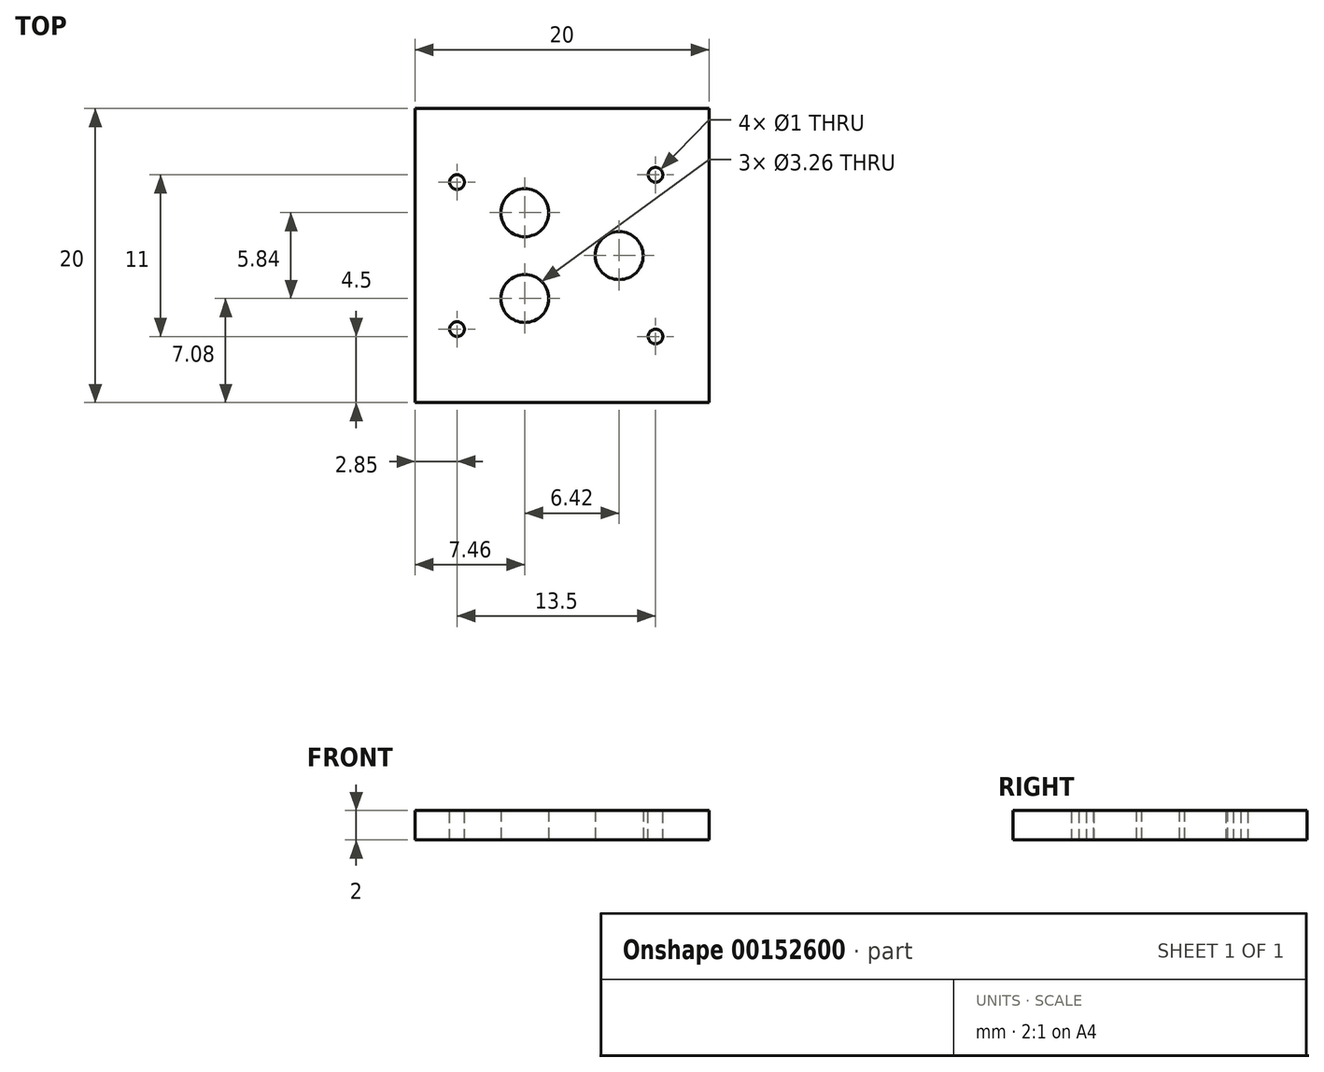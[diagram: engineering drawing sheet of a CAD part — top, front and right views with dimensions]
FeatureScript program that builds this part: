
annotation { "Feature Type Name" : "Feature", "Feature Type Description" : "" }
export const myFeature = defineFeature(function(context is Context, id is Id, definition is map)
    precondition{}
    {
        {
            var Q0;
            Q0=qCreatedBy(makeId("Top.planeOp"),FACE);
            var sketch = newSketch(context, id + "F0", { "sketchPlane" : qUnion([Q0])});
            skLineSegment(sketch, "E0.bottom", {"start": v(-10, 10) * mm, "end": v(10, 10) * mm});
            skLineSegment(sketch, "E0.top", {"start": v(-10, -10) * mm, "end": v(10, -10) * mm});
            skLineSegment(sketch, "E0.left", {"start": v(-10, 10) * mm, "end": v(-10, -10) * mm});
            skLineSegment(sketch, "E0.right", {"start": v(10, 10) * mm, "end": v(10, -10) * mm});
            skPoint(sketch, "E0.middle", {"position": v(0, 0) * mm});
            skCircle(sketch, "E1", {"center": v(-2.54, 2.92) * mm, "radius": 1.63 * mm});
            skCircle(sketch, "E2", {"center": v(-2.54, -2.92) * mm, "radius": 1.63 * mm});
            skCircle(sketch, "E3", {"center": v(3.88, 0) * mm, "radius": 1.63 * mm});
            skSolve(sketch);
        }
        {
            var Q0;
            Q0=makeQuery(id+"F0.imprint","IMPRINT",FACE,{"disambiguationData":[TD([[makeQuery(id+"F0.imprint","IMPRINT",EDGE,{"derivedFrom":sQuery(id+"F0.wireOp",EDGE,"E0.bottom")}),-1.0]])]});
            extrude(context, id + "F1", {"entities" : qUnion([Q0]), "depth" : 2 * mm});
        }
        {
            var Q0;
            Q0=makeQuery(id+"F1.opExtrude","CAP_FACE",FACE,{"disambiguationData":[OSD([sQuery(id+"F0.wireOp",EDGE,"E0.bottom"),sQuery(id+"F0.wireOp",EDGE,"E0.top"),sQuery(id+"F0.wireOp",EDGE,"E0.left"),sQuery(id+"F0.wireOp",EDGE,"E0.right"),sQuery(id+"F0.wireOp",EDGE,"E1"),sQuery(id+"F0.wireOp",EDGE,"E2"),sQuery(id+"F0.wireOp",EDGE,"E3")])],"isStart":false});
            var sketch = newSketch(context, id + "F2", { "sketchPlane" : qUnion([Q0])});
            skLineSegment(sketch, "E4.bottom", {"start": v(5, 5) * mm, "end": v(-5, 5) * mm});
            skLineSegment(sketch, "E4.top", {"start": v(5, -5) * mm, "end": v(-5, -5) * mm});
            skLineSegment(sketch, "E4.right", {"start": v(-5, 5) * mm, "end": v(-5, -5) * mm});
            skPoint(sketch, "E4.middle", {"position": v(0, 0) * mm});
            skLineSegment(sketch, "E5", {"start": v(5, 5) * mm, "end": v(6, 5) * mm});
            skLineSegment(sketch, "E6", {"start": v(6, 5) * mm, "end": v(6, -5) * mm});
            skLineSegment(sketch, "E7", {"start": v(6, -5) * mm, "end": v(5, -5) * mm});
            skPoint(sketch, "E8", {"position": v(6.35, 5.5) * mm});
            skPoint(sketch, "E9", {"position": v(-7.15, 5) * mm});
            skLineSegment(sketch, "E10", {"start": v(0, 0) * mm, "end": v(1.26, 0) * mm});
            skPoint(sketch, "E11.MirrorP", {"position": v(6.35, -5.5) * mm});
            skPoint(sketch, "E12.MirrorP", {"position": v(-7.15, -5) * mm});
            skSolve(sketch);
        }
        {
            var Q0;
            Q0=sQuery(id+"F2.wireOp",VERTEX,"E8");
            var Q1;
            Q1=sQuery(id+"F2.wireOp",VERTEX,"E11.MirrorP");
            var Q2;
            Q2=sQuery(id+"F2.wireOp",VERTEX,"E12.MirrorP");
            var Q3;
            Q3=sQuery(id+"F2.wireOp",VERTEX,"E9");
            var Q4;
            Q4=makeQuery(id+"F1.opExtrude","SWEPT_BODY",BODY,{"disambiguationData":[OSD([sQuery(id+"F0.wireOp",EDGE,"E0.bottom"),sQuery(id+"F0.wireOp",EDGE,"E0.top"),sQuery(id+"F0.wireOp",EDGE,"E0.left"),sQuery(id+"F0.wireOp",EDGE,"E0.right"),sQuery(id+"F0.wireOp",EDGE,"E1"),sQuery(id+"F0.wireOp",EDGE,"E2"),sQuery(id+"F0.wireOp",EDGE,"E3")])]});
            hole(context, id + "F3", {"style" : HoleStyle.SIMPLE, "endStyle" : HoleEndStyle.THROUGH, "holeDiameter" : 1 * mm, "startFromSketch" : true, "locations" : qUnion([Q0, Q1, Q2, Q3]), "scope" : qUnion([Q4]), "isTappedThrough" : true});
        }
    });
